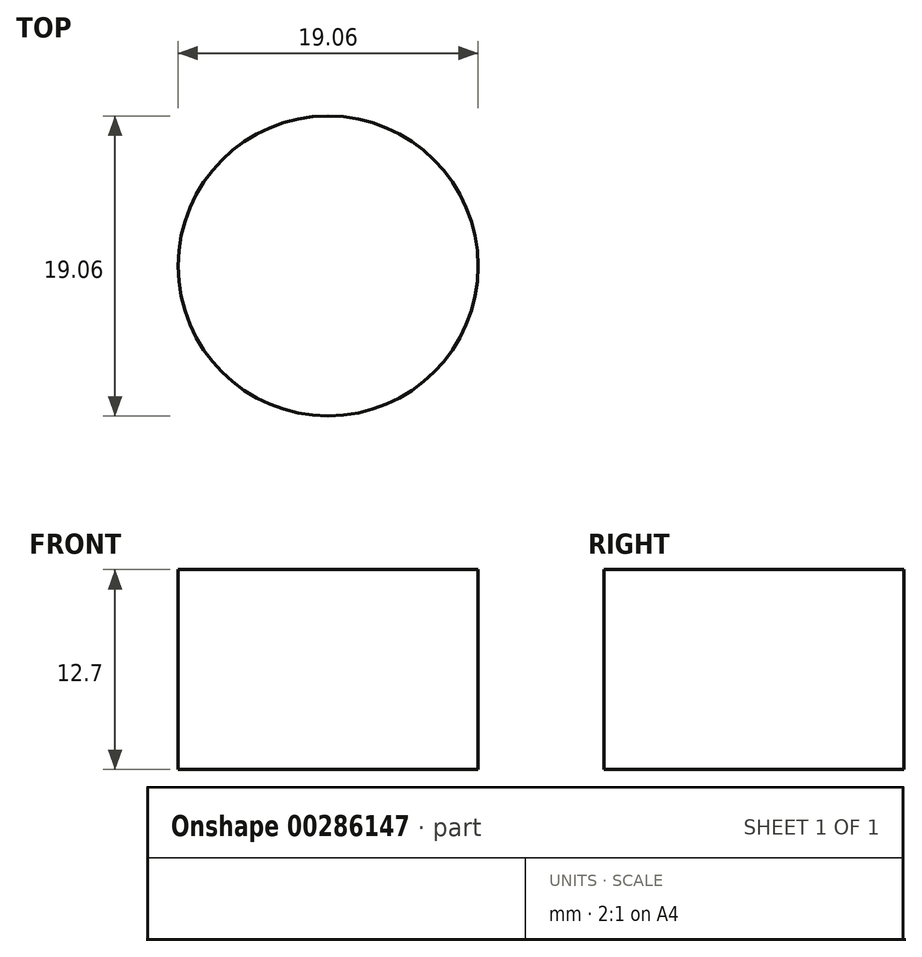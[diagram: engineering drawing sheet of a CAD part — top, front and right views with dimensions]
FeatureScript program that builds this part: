
annotation { "Feature Type Name" : "Feature", "Feature Type Description" : "" }
export const myFeature = defineFeature(function(context is Context, id is Id, definition is map)
    precondition{}
    {
        {
            var Q0;
            Q0=qCreatedBy(makeId("Top.planeOp"),FACE);
            var sketch = newSketch(context, id + "F0", { "sketchPlane" : qUnion([Q0])});
            skCircle(sketch, "E0", {"center": v(0, 0) * mm, "radius": 9.53 * mm});
            skSolve(sketch);
        }
        {
            var Q0;
            Q0=makeQuery(id+"F0.imprint","IMPRINT",FACE,{"disambiguationData":[TD([[makeQuery(id+"F0.imprint","IMPRINT",EDGE,{"derivedFrom":sQuery(id+"F0.wireOp",EDGE,"E0")}),1.0]])]});
            extrude(context, id + "F1", {"entities" : qUnion([Q0]), "depth" : 12.7 * mm});
        }
    });
